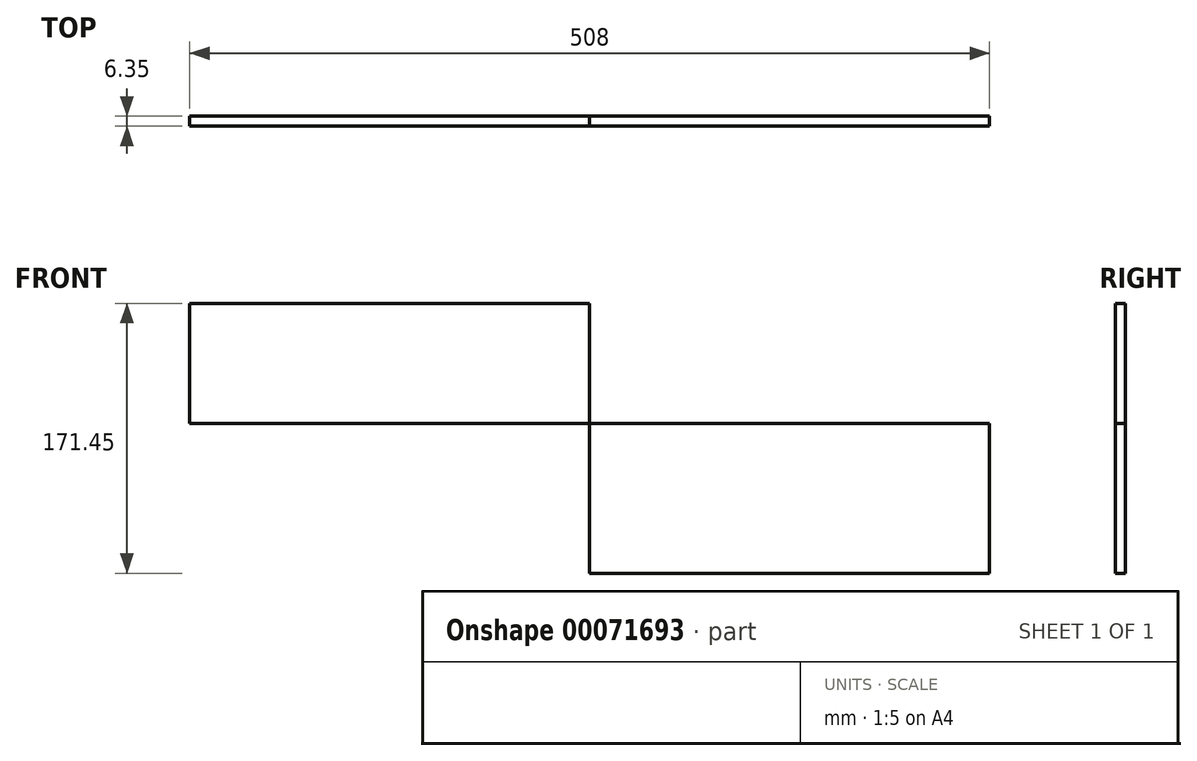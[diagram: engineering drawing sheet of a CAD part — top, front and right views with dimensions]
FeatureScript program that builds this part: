
annotation { "Feature Type Name" : "Feature", "Feature Type Description" : "" }
export const myFeature = defineFeature(function(context is Context, id is Id, definition is map)
    precondition{}
    {
        {
            var Q0;
            Q0=qCreatedBy(makeId("Front.planeOp"),FACE);
            var sketch = newSketch(context, id + "F0", { "sketchPlane" : qUnion([Q0])});
            skLineSegment(sketch, "E0.bottom", {"start": v(0, 0) * mm, "end": v(-254, 0) * mm});
            skLineSegment(sketch, "E0.top", {"start": v(0, 76.2) * mm, "end": v(-254, 76.2) * mm});
            skLineSegment(sketch, "E0.left", {"start": v(0, 0) * mm, "end": v(0, 76.2) * mm});
            skLineSegment(sketch, "E0.right", {"start": v(-254, 0) * mm, "end": v(-254, 76.2) * mm});
            skLineSegment(sketch, "E1.bottom", {"start": v(0, 0) * mm, "end": v(254, 0) * mm});
            skLineSegment(sketch, "E1.top", {"start": v(0, -95.25) * mm, "end": v(254, -95.25) * mm});
            skLineSegment(sketch, "E1.left", {"start": v(0, 0) * mm, "end": v(0, -95.25) * mm});
            skLineSegment(sketch, "E1.right", {"start": v(254, 0) * mm, "end": v(254, -95.25) * mm});
            skSolve(sketch);
        }
        {
            var Q0;
            Q0=makeQuery(id+"F0.imprint","IMPRINT",FACE,{"disambiguationData":[TD([[makeQuery(id+"F0.imprint","IMPRINT",EDGE,{"derivedFrom":sQuery(id+"F0.wireOp",EDGE,"E0.bottom")}),-1.0]])]});
            var Q1;
            Q1=makeQuery(id+"F0.imprint","IMPRINT",FACE,{"disambiguationData":[TD([[makeQuery(id+"F0.imprint","IMPRINT",EDGE,{"derivedFrom":sQuery(id+"F0.wireOp",EDGE,"E1.bottom")}),-1.0]])]});
            extrude(context, id + "F1", {"entities" : qUnion([Q0, Q1]), "depth" : 6.35 * mm});
        }
    });
